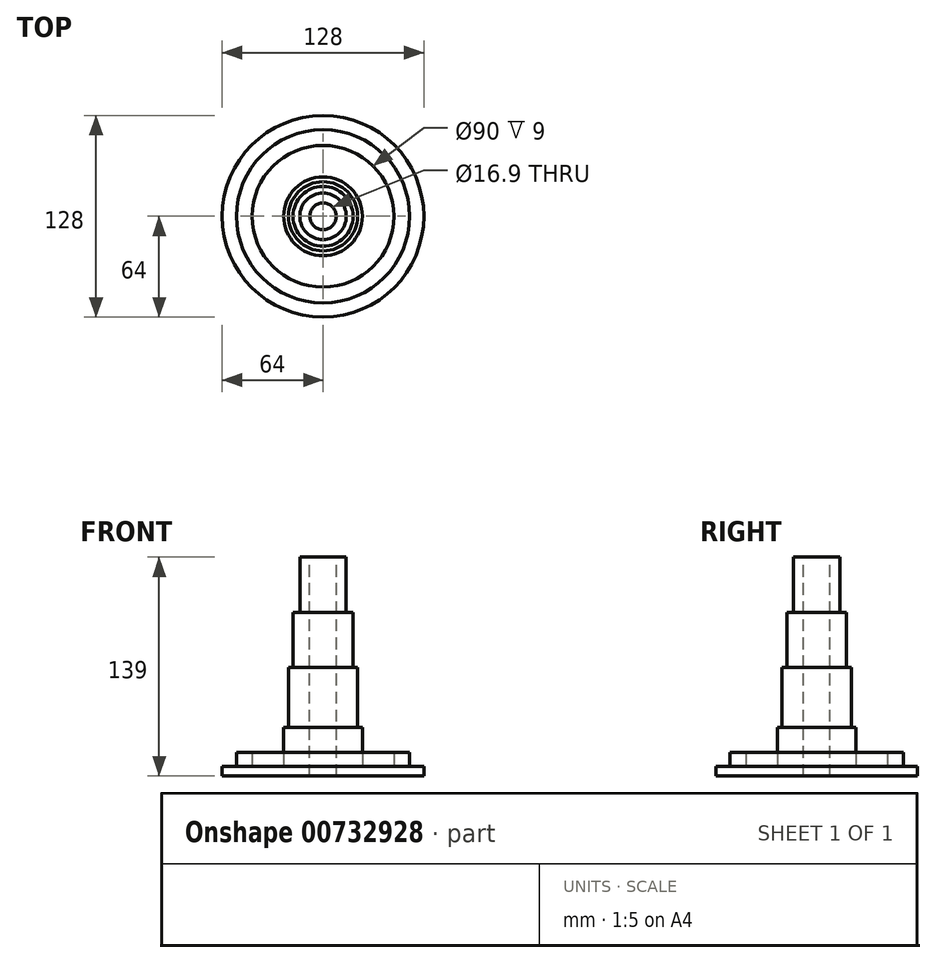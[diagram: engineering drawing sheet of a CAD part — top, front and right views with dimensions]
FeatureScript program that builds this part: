
annotation { "Feature Type Name" : "Feature", "Feature Type Description" : "" }
export const myFeature = defineFeature(function(context is Context, id is Id, definition is map)
    precondition{}
    {
        {
            var Q0;
            Q0=qCreatedBy(makeId("Top.planeOp"),FACE);
            var sketch = newSketch(context, id + "F0", { "sketchPlane" : qUnion([Q0])});
            skCircle(sketch, "E0", {"center": v(0, 0) * mm, "radius": 55 * mm});
            skCircle(sketch, "E1", {"center": v(0, 0) * mm, "radius": 64 * mm});
            skSolve(sketch);
        }
        {
            var Q0;
            Q0=makeQuery(id+"F0.imprint","IMPRINT",FACE,{"disambiguationData":[TD([[makeQuery(id+"F0.imprint","IMPRINT",EDGE,{"derivedFrom":sQuery(id+"F0.wireOp",EDGE,"E0")}),-1.0]])]});
            var Q1;
            Q1=makeQuery(id+"F0.imprint","IMPRINT",FACE,{"disambiguationData":[TD([[makeQuery(id+"F0.imprint","IMPRINT",EDGE,{"derivedFrom":sQuery(id+"F0.wireOp",EDGE,"E0")}),1.0]])]});
            extrude(context, id + "F1", {"entities" : qUnion([Q0, Q1]), "depth" : 6 * mm, "offsetDistance" : 25 * mm});
        }
        {
            var Q0;
            Q0=makeQuery(id+"F1.opExtrude","CAP_FACE",FACE,{"disambiguationData":[OSD([sQuery(id+"F0.wireOp",EDGE,"E1")])],"isStart":false});
            var sketch = newSketch(context, id + "F2", { "sketchPlane" : qUnion([Q0])});
            skCircle(sketch, "E2", {"center": v(0, 0) * mm, "radius": 55 * mm});
            skCircle(sketch, "E3", {"center": v(0, 0) * mm, "radius": 45 * mm});
            skSolve(sketch);
        }
        {
            var Q0;
            Q0=makeQuery(id+"F2.imprint","IMPRINT",FACE,{"disambiguationData":[TD([[makeQuery(id+"F2.imprint","IMPRINT",EDGE,{"derivedFrom":sQuery(id+"F2.wireOp",EDGE,"E2")}),1.0]])]});
            extrude(context, id + "F3", {"entities" : qUnion([Q0]), "operationType" : NewBodyOperationType.ADD, "depth" : 9 * mm, "offsetDistance" : 25 * mm});
        }
        {
            var Q0;
            Q0=makeQuery(id+"F3.boolean.opBoolean","SPLIT",FACE,{"disambiguationData":[TD([makeQuery(id+"F3.opExtrude","SWEPT_FACE",FACE,{"disambiguationData":[OSD([sQuery(id+"F2.wireOp",EDGE,"E3")])]})])],"derivedFrom":makeQuery(id+"F1.opExtrude","CAP_FACE",FACE,{"disambiguationData":[OSD([sQuery(id+"F0.wireOp",EDGE,"E1")])],"isStart":false})});
            var sketch = newSketch(context, id + "F4", { "sketchPlane" : qUnion([Q0])});
            skCircle(sketch, "E4", {"center": v(0, 0) * mm, "radius": 25 * mm});
            skSolve(sketch);
        }
        {
            var Q0;
            Q0=makeQuery(id+"F4.imprint","IMPRINT",FACE,{"disambiguationData":[TD([[makeQuery(id+"F4.imprint","IMPRINT",EDGE,{"derivedFrom":sQuery(id+"F4.wireOp",EDGE,"E4")}),1.0]])]});
            extrude(context, id + "F5", {"entities" : qUnion([Q0]), "operationType" : NewBodyOperationType.ADD, "depth" : 25 * mm, "offsetDistance" : 25 * mm});
        }
        {
            var Q0;
            Q0=makeQuery(id+"F5.opExtrude","CAP_FACE",FACE,{"disambiguationData":[OSD([sQuery(id+"F4.wireOp",EDGE,"E4")])],"isStart":false});
            var sketch = newSketch(context, id + "F6", { "sketchPlane" : qUnion([Q0])});
            skCircle(sketch, "E5", {"center": v(0, 0) * mm, "radius": 22 * mm});
            skSolve(sketch);
        }
        {
            var Q0;
            Q0 = qSketchRegion(id + "F6", true);
            extrude(context, id + "F7", {"entities" : qUnion([Q0]), "operationType" : NewBodyOperationType.ADD, "depth" : 38 * mm, "offsetDistance" : 25 * mm});
        }
        {
            var Q0;
            Q0=makeQuery(id+"F7.opExtrude","CAP_FACE",FACE,{"disambiguationData":[OSD([sQuery(id+"F6.wireOp",EDGE,"E5")])],"isStart":false});
            var sketch = newSketch(context, id + "F8", { "sketchPlane" : qUnion([Q0])});
            skCircle(sketch, "E6", {"center": v(0, 0) * mm, "radius": 19 * mm});
            skSolve(sketch);
        }
        {
            var Q0;
            Q0 = qSketchRegion(id + "F8", true);
            extrude(context, id + "F9", {"entities" : qUnion([Q0]), "operationType" : NewBodyOperationType.ADD, "depth" : 35 * mm, "offsetDistance" : 25 * mm});
        }
        {
            var Q0;
            Q0=makeQuery(id+"F9.opExtrude","CAP_FACE",FACE,{"disambiguationData":[OSD([sQuery(id+"F8.wireOp",EDGE,"E6")])],"isStart":false});
            var sketch = newSketch(context, id + "F10", { "sketchPlane" : qUnion([Q0])});
            skCircle(sketch, "E7", {"center": v(0, 0) * mm, "radius": 14.75 * mm});
            skSolve(sketch);
        }
        {
            var Q0;
            Q0=makeQuery(id+"F10.imprint","IMPRINT",FACE,{"disambiguationData":[TD([[makeQuery(id+"F10.imprint","IMPRINT",EDGE,{"derivedFrom":sQuery(id+"F10.wireOp",EDGE,"E7")}),1.0]])]});
            extrude(context, id + "F11", {"entities" : qUnion([Q0]), "operationType" : NewBodyOperationType.ADD, "depth" : 35 * mm, "offsetDistance" : 25 * mm});
        }
        {
            var Q0;
            Q0=makeQuery(id+"F11.opExtrude","CAP_FACE",FACE,{"disambiguationData":[OSD([sQuery(id+"F10.wireOp",EDGE,"E7")])],"isStart":false});
            var sketch = newSketch(context, id + "F12", { "sketchPlane" : qUnion([Q0])});
            skCircle(sketch, "E8", {"center": v(0, 0) * mm, "radius": 8.45 * mm});
            skSolve(sketch);
        }
        {
            var Q0;
            Q0=makeQuery(id+"F12.imprint","IMPRINT",FACE,{"disambiguationData":[TD([[makeQuery(id+"F12.imprint","IMPRINT",EDGE,{"derivedFrom":sQuery(id+"F12.wireOp",EDGE,"E8")}),1.0]])]});
            extrude(context, id + "F13", {"entities" : qUnion([Q0]), "operationType" : NewBodyOperationType.REMOVE, "oppositeDirection" : true, "depth" : 200 * mm, "offsetDistance" : 25 * mm});
        }
    });
